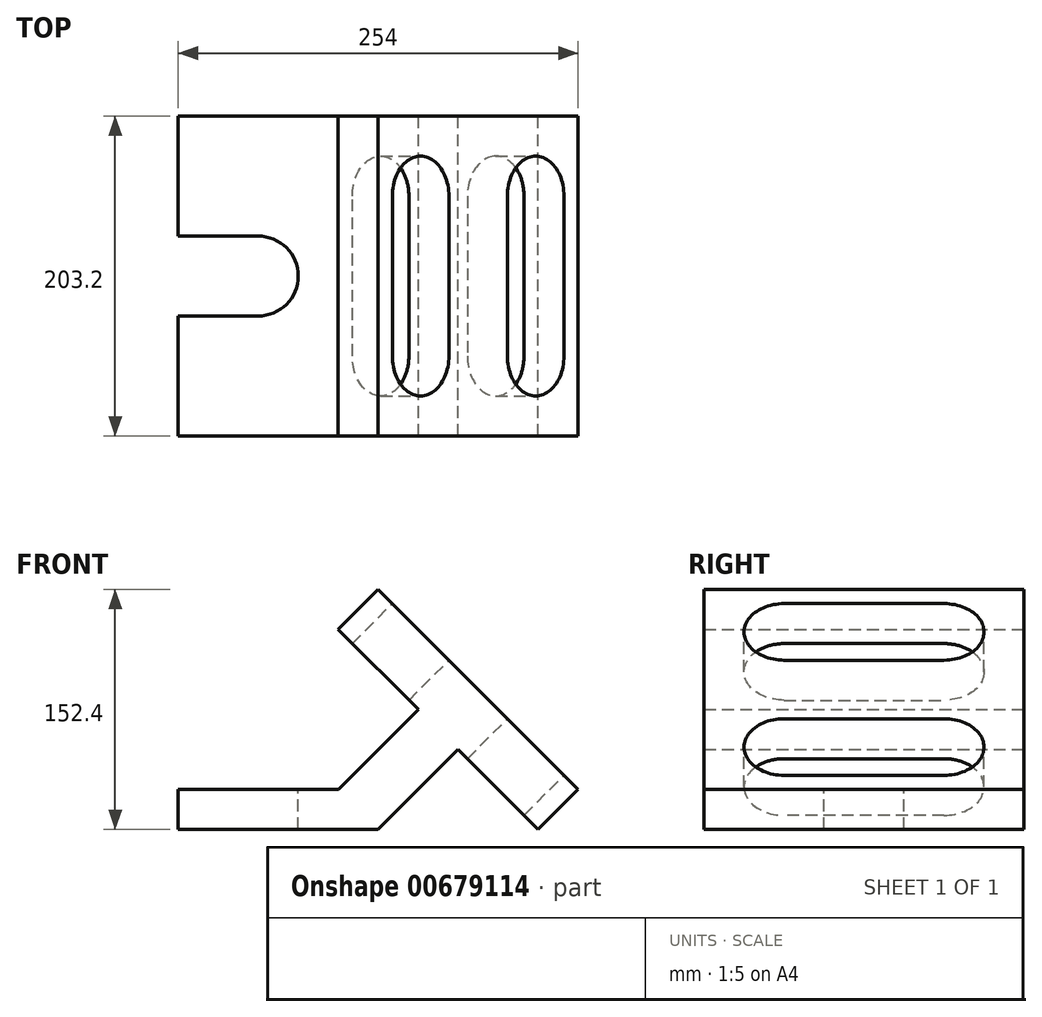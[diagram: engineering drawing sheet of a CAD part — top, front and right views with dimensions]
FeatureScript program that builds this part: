
annotation { "Feature Type Name" : "Feature", "Feature Type Description" : "" }
export const myFeature = defineFeature(function(context is Context, id is Id, definition is map)
    precondition{}
    {
        {
            var Q0;
            Q0=qCreatedBy(makeId("Front.planeOp"),FACE);
            var sketch = newSketch(context, id + "F0", { "sketchPlane" : qUnion([Q0])});
            skLineSegment(sketch, "E0", {"start": v(0, 0) * mm, "end": v(127, 0) * mm});
            skLineSegment(sketch, "E1", {"start": v(177.8, 50.8) * mm, "end": v(127, 0) * mm});
            skLineSegment(sketch, "E2", {"start": v(177.8, 50.8) * mm, "end": v(228.6, 0) * mm});
            skLineSegment(sketch, "E3.0", {"start": v(152.48, 76.12) * mm, "end": v(101.75, 25.4) * mm});
            skLineSegment(sketch, "E4.0", {"start": v(127, 152.4) * mm, "end": v(254, 25.4) * mm});
            skLineSegment(sketch, "E5", {"start": v(0, 25.4) * mm, "end": v(0, 0) * mm});
            skLineSegment(sketch, "E6", {"start": v(0, 25.4) * mm, "end": v(101.75, 25.4) * mm});
            skLineSegment(sketch, "E7", {"start": v(152.48, 76.12) * mm, "end": v(101.6, 127) * mm});
            skLineSegment(sketch, "E8", {"start": v(228.6, 0) * mm, "end": v(254, 25.4) * mm});
            skLineSegment(sketch, "E9", {"start": v(127, 152.4) * mm, "end": v(101.6, 127) * mm});
            skSolve(sketch);
        }
        {
            var Q0;
            Q0=makeQuery(id+"F0.imprint","IMPRINT",FACE,{"disambiguationData":[TD([[makeQuery(id+"F0.imprint","IMPRINT",EDGE,{"derivedFrom":sQuery(id+"F0.wireOp",EDGE,"E0")}),1.0]])]});
            extrude(context, id + "F1", {"entities" : qUnion([Q0]), "endBound" : BoundingType.SYMMETRIC, "depth" : 203.2 * mm, "offsetDistance" : 25.4 * mm});
        }
        {
            var Q0;
            Q0=makeQuery(id+"F1.opExtrude","SWEPT_FACE",FACE,{"disambiguationData":[OSD([sQuery(id+"F0.wireOp",EDGE,"E4.0")])]});
            var sketch = newSketch(context, id + "F2", { "sketchPlane" : qUnion([Q0])});
            skLineSegment(sketch, "E10", {"start": v(50.8, 5.26) * mm, "end": v(-50.8, 5.26) * mm});
            skLineSegment(sketch, "E11", {"start": v(50.8, -148.94) * mm, "end": v(-50.8, -148.94) * mm});
            skLineSegment(sketch, "E12.0", {"start": v(50.8, -45.54) * mm, "end": v(-50.8, -45.54) * mm});
            skLineSegment(sketch, "E13.0", {"start": v(50.8, -98.14) * mm, "end": v(-50.8, -98.14) * mm});
            skArc(sketch, "E14", {"start": v(-50.8, -45.54) * mm, "mid": v(-76.2, -20.14) * mm, "end": v(-50.8, 5.26) * mm});
            skArc(sketch, "E15", {"start": v(50.8, 5.26) * mm, "mid": v(76.2, -20.14) * mm, "end": v(50.8, -45.54) * mm});
            skArc(sketch, "E16", {"start": v(50.8, -98.14) * mm, "mid": v(76.2, -123.54) * mm, "end": v(50.8, -148.94) * mm});
            skArc(sketch, "E17", {"start": v(-50.8, -98.14) * mm, "mid": v(-76.2, -123.54) * mm, "end": v(-50.8, -148.94) * mm});
            skSolve(sketch);
        }
        {
            var Q0;
            Q0=makeQuery(id+"F1.opExtrude","SWEPT_FACE",FACE,{"disambiguationData":[OSD([sQuery(id+"F0.wireOp",EDGE,"E6")])]});
            var sketch = newSketch(context, id + "F3", { "sketchPlane" : qUnion([Q0])});
            skLineSegment(sketch, "E18", {"start": v(0, 25.4) * mm, "end": v(50.8, 25.4) * mm});
            skLineSegment(sketch, "E19", {"start": v(0, -25.4) * mm, "end": v(50.8, -25.4) * mm});
            skArc(sketch, "E20", {"start": v(50.8, 25.4) * mm, "mid": v(76.2, 0) * mm, "end": v(50.8, -25.4) * mm});
            skLineSegment(sketch, "E21", {"start": v(0, 25.4) * mm, "end": v(0, -25.4) * mm});
            skSolve(sketch);
        }
        {
            var Q0;
            Q0=makeQuery(id+"F3.imprint","IMPRINT",FACE,{"disambiguationData":[TD([[makeQuery(id+"F3.imprint","IMPRINT",EDGE,{"derivedFrom":sQuery(id+"F3.wireOp",EDGE,"E18")}),-1.0]])]});
            extrude(context, id + "F4", {"entities" : qUnion([Q0]), "operationType" : NewBodyOperationType.REMOVE, "endBound" : BoundingType.THROUGH_ALL, "oppositeDirection" : true, "depth" : 25.4 * mm, "offsetDistance" : 25.4 * mm});
        }
        {
            var Q0;
            Q0=makeQuery(id+"F2.imprint","IMPRINT",FACE,{"disambiguationData":[TD([[makeQuery(id+"F2.imprint","IMPRINT",EDGE,{"derivedFrom":sQuery(id+"F2.wireOp",EDGE,"E10")}),1.0]])]});
            var Q1;
            Q1=makeQuery(id+"F2.imprint","IMPRINT",FACE,{"disambiguationData":[TD([[makeQuery(id+"F2.imprint","IMPRINT",EDGE,{"derivedFrom":sQuery(id+"F2.wireOp",EDGE,"E11")}),-1.0]])]});
            extrude(context, id + "F5", {"entities" : qUnion([Q0, Q1]), "operationType" : NewBodyOperationType.REMOVE, "oppositeDirection" : true, "depth" : 76.2 * mm, "offsetDistance" : 25.4 * mm});
        }
    });
